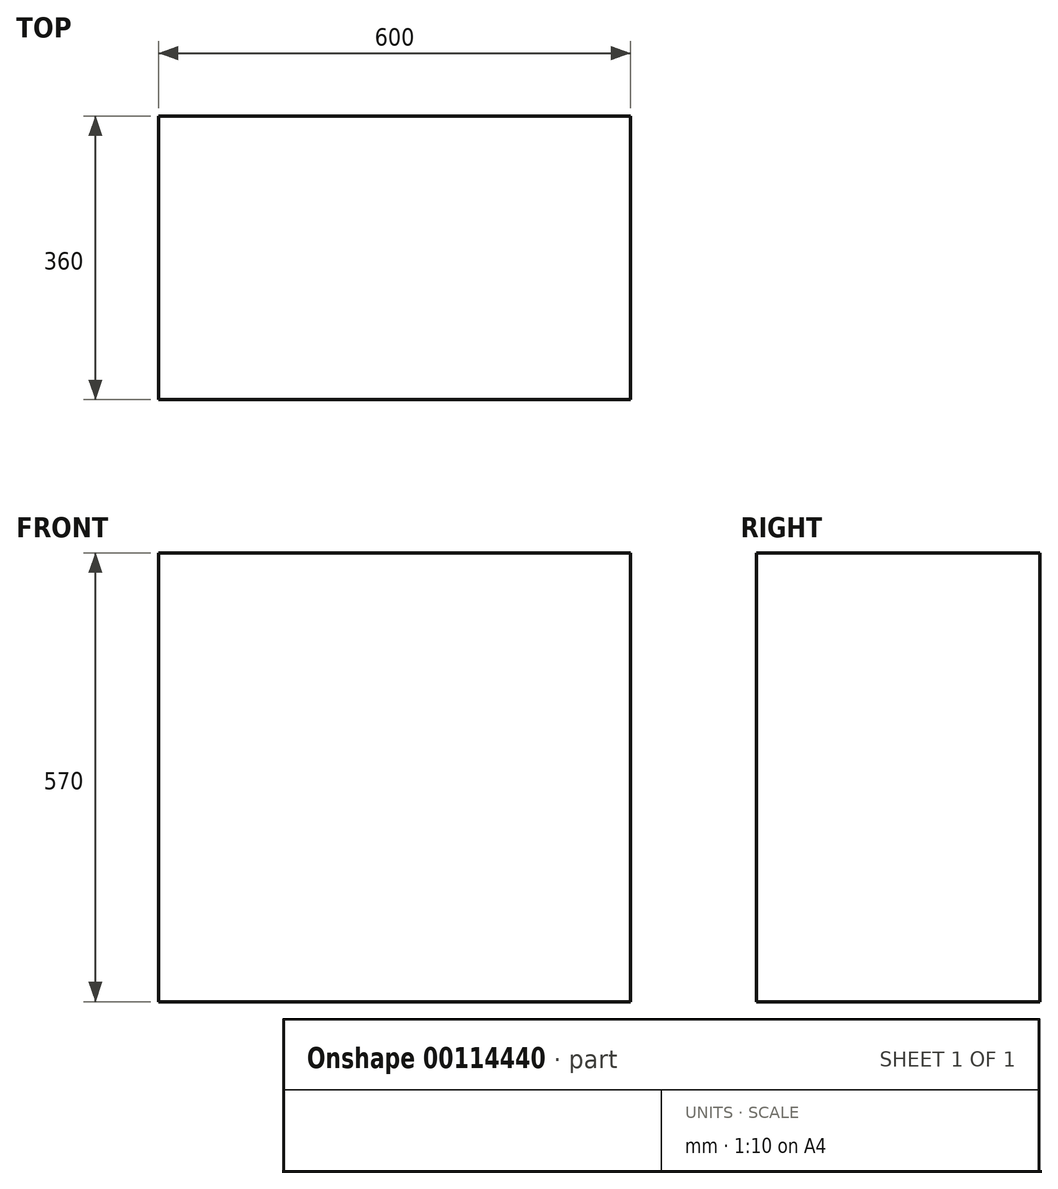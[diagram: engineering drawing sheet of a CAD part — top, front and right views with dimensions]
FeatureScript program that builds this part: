
annotation { "Feature Type Name" : "Feature", "Feature Type Description" : "" }
export const myFeature = defineFeature(function(context is Context, id is Id, definition is map)
    precondition{}
    {
        {
            var Q0;
            Q0=qCreatedBy(makeId("Front.planeOp"),FACE);
            var sketch = newSketch(context, id + "F0", { "sketchPlane" : qUnion([Q0])});
            skLineSegment(sketch, "E0.bottom", {"start": v(-300, -285) * mm, "end": v(300, -285) * mm});
            skLineSegment(sketch, "E0.top", {"start": v(-300, 285) * mm, "end": v(300, 285) * mm});
            skLineSegment(sketch, "E0.left", {"start": v(-300, -285) * mm, "end": v(-300, 285) * mm});
            skLineSegment(sketch, "E0.right", {"start": v(300, -285) * mm, "end": v(300, 285) * mm});
            skPoint(sketch, "E0.middle", {"position": v(0, 0) * mm});
            skSolve(sketch);
        }
        {
            var Q0;
            Q0 = qSketchRegion(id + "F0", true);
            extrude(context, id + "F1", {"entities" : qUnion([Q0]), "depth" : 360 * mm});
        }
    });
